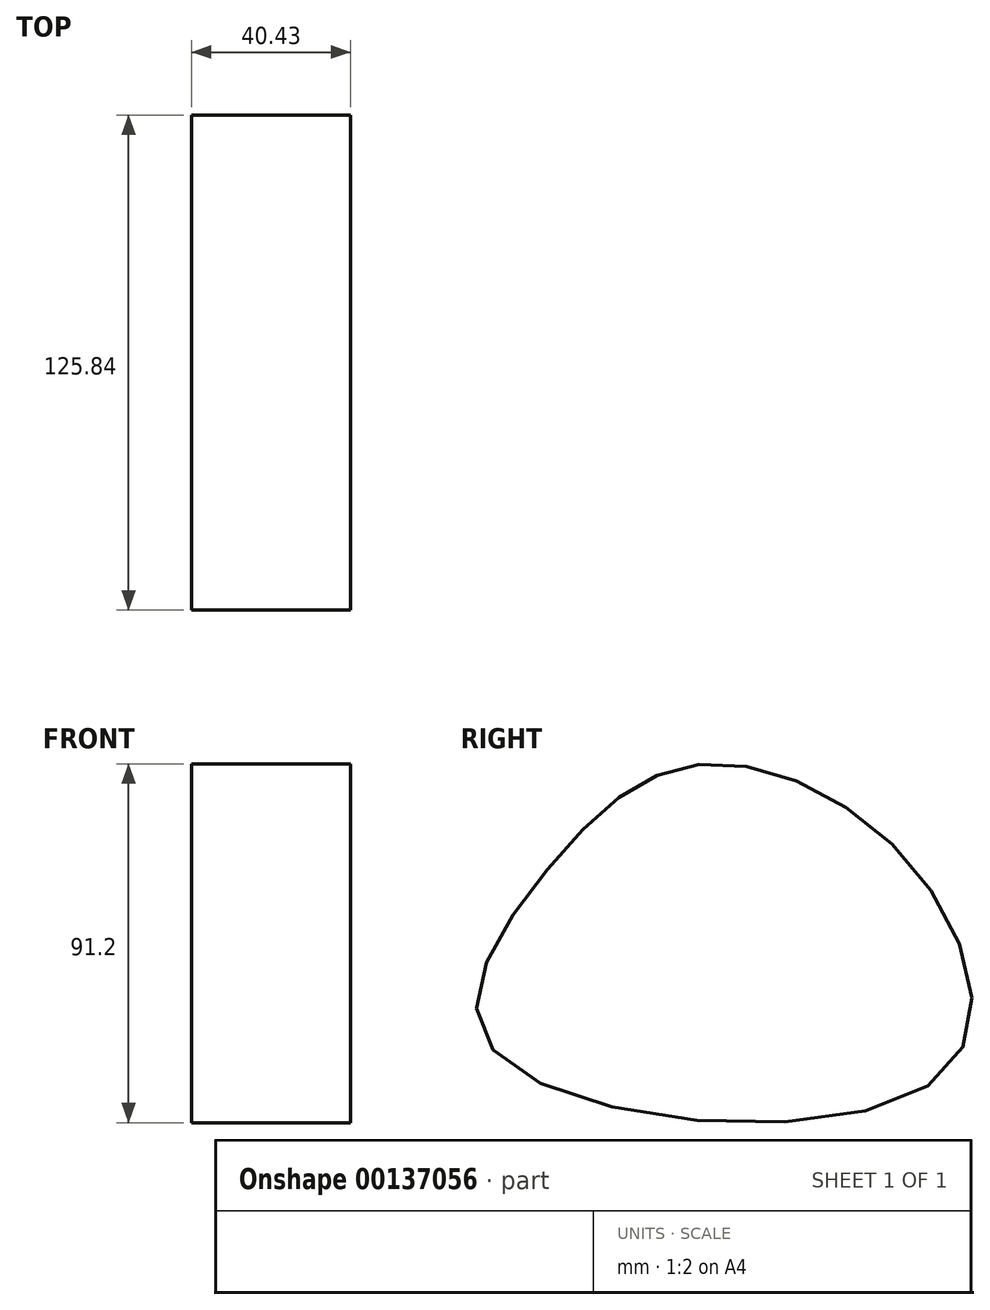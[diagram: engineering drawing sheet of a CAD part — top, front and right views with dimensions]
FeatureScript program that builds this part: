
annotation { "Feature Type Name" : "Feature", "Feature Type Description" : "" }
export const myFeature = defineFeature(function(context is Context, id is Id, definition is map)
    precondition{}
    {
        {
            var Q0;
            Q0=qCreatedBy(makeId("Right.planeOp"),FACE);
            var sketch = newSketch(context, id + "F0", { "sketchPlane" : qUnion([Q0])});
            skFitSpline(sketch, "E0", {"points": [v(-58.07, -19.05) * mm, v(-43.62, 27.46) * mm, v(-5.52, 53.47) * mm, v(48.87, 27.2) * mm, v(54.65, -26.67) * mm, v(-58.07, -19.05) * mm]});
            skSolve(sketch);
        }
        {
            var Q0;
            Q0=makeQuery(id+"F0.imprint","IMPRINT",FACE,{"disambiguationData":[TD([[makeQuery(id+"F0.imprint","IMPRINT",EDGE,{"derivedFrom":sQuery(id+"F0.wireOp",EDGE,"E0")}),-1.0]])]});
            var Q1;
            Q1=sQuery(id+"F0.wireOp",EDGE,"E0");
            extrude(context, id + "F1", {"entities" : qUnion([Q0]), "surfaceEntities" : qUnion([Q1]), "depth" : 40.43 * mm});
        }
    });
